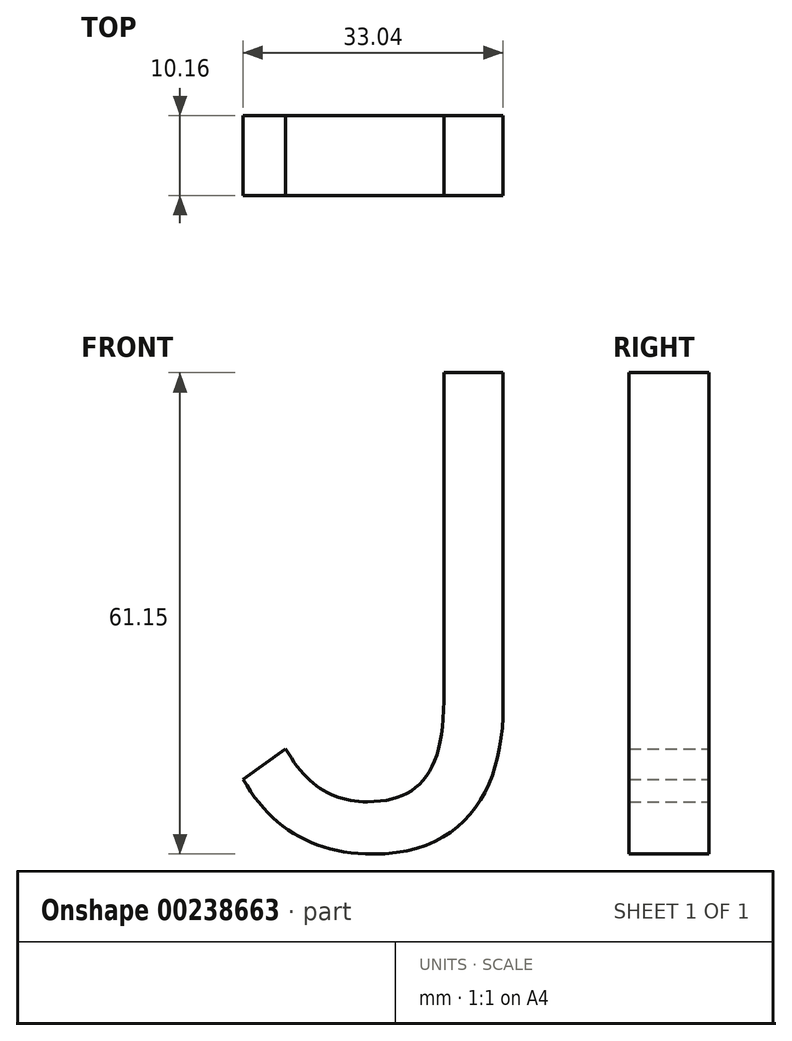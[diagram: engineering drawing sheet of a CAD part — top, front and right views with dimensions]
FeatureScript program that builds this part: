
annotation { "Feature Type Name" : "Feature", "Feature Type Description" : "" }
export const myFeature = defineFeature(function(context is Context, id is Id, definition is map)
    precondition{}
    {
        {
            var Q0;
            Q0=qCreatedBy(makeId("Front.planeOp"),FACE);
            var sketch = newSketch(context, id + "F0", { "sketchPlane" : qUnion([Q0])});
            skText(sketch, "E0", { "text": "J", "fontName": "NotoSansCJKsc-Regular.otf"});
            const initialGuessF0  = {"E0": [-0.02563, -0.02686, 1, 0, 0.05903]};
            skSetInitialGuess(sketch, initialGuessF0);
            skSolve(sketch);
        }
        {
            var Q0;
            Q0 = qSketchRegion(id + "F0", true);
            extrude(context, id + "F1", {"entities" : qUnion([Q0]), "depth" : 10.16 * mm});
        }
    });
